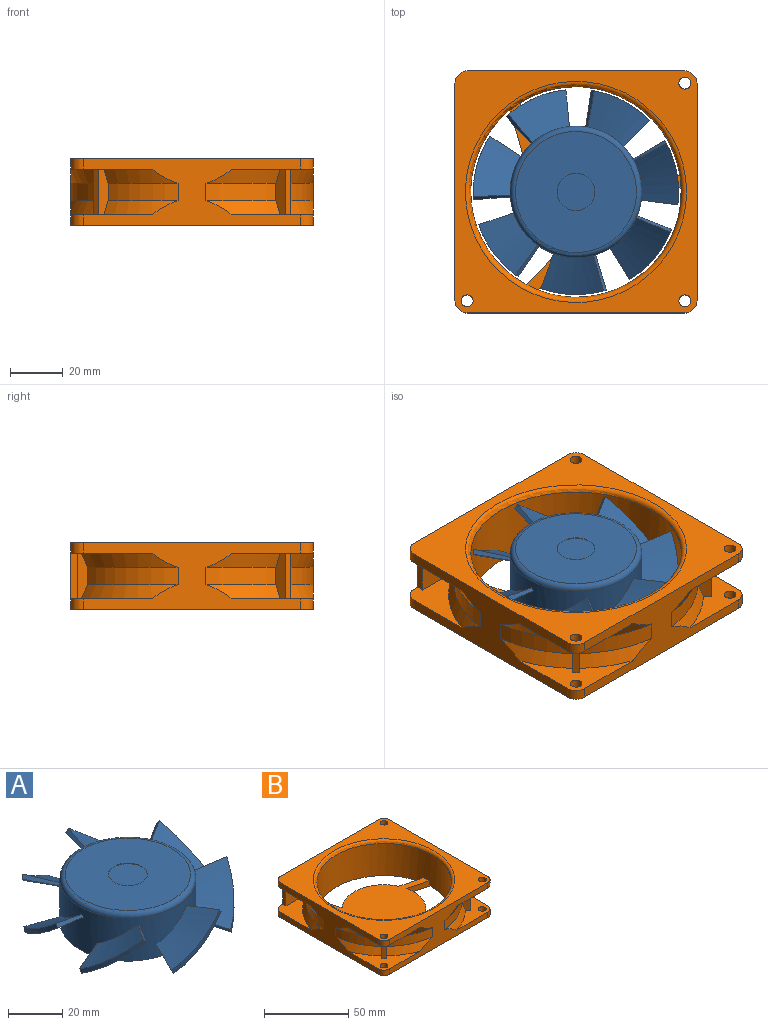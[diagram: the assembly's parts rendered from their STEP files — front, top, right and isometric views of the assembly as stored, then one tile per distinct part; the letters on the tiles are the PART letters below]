
ASSEMBLY  parts=2 mates=1
PART A: 41 faces, bbox 82.4x80.7x21.5 mm
  f0: cylinder r=39mm len=24.46mm, axis (0,0,-1), area 55.4mm2, adj f23,f24,f25,f26
  f1: cylinder r=7.14mm len=14.28mm, axis (0,0,1), area 11.2mm2, adj f32,f33
  f2: torus R=23mm, axis (0,0,-1), area 479.1mm2, adj f3,f33
  f3: cylinder r=25mm len=50mm, axis (0,0,1), area 2885.5mm2, adj f2,f4,f6,f7,f8,f9,f10,f11
  f4: plane 50x50mm, normal (0,0,-1), area 1963.5mm2, adj f3
  f5: cylinder r=39mm len=20.03mm, axis (0,0,-1), area 56.1mm2, adj f6,f7,f8,f9
  f6: bspline ~25.09x24.29mm, area 335.7mm2, adj f3,f5,f7,f9
  f7: plane 11.91x8.96mm, normal (0.71,-0.36,0.6), area 22.3mm2, adj f3,f5,f6,f8
  f8: bspline ~38.56x33.79mm, area 340.4mm2, adj f3,f5,f7,f9
  f9: plane 13.5x5.1mm, normal (-0.2,0.88,-0.44), area 22.3mm2, adj f3,f5,f6,f8
  f10: bspline ~24.11x19.98mm, area 335.6mm2, adj f3,f11,f13,f39
  f11: plane 14.06x4.13mm, normal (0.16,-0.78,0.6), area 22.3mm2, adj f3,f10,f12,f39
  f12: bspline ~41.55x24.68mm, area 340.4mm2, adj f3,f11,f13,f39
  f13: plane 12.23x8.31mm, normal (0.56,0.7,-0.44), area 22.3mm2, adj f3,f10,f12,f39
  f14: cylinder r=39mm len=22.82mm, axis (0,0,-1), area 56.1mm2, adj f15,f16,f17,f18
  f15: bspline ~24.34x22.05mm, area 335.7mm2, adj f3,f14,f16,f18
  f16: plane 11.14x9.97mm, normal (-0.51,-0.61,0.6), area 22.3mm2, adj f3,f14,f15,f17
  f17: bspline ~40.56x27.69mm, area 340.4mm2, adj f3,f14,f16,f18
  f18: plane 14x4.39mm, normal (0.9,0,-0.44), area 22.3mm2, adj f3,f14,f15,f17
  f19: bspline ~40.48x30.08mm, area 335.6mm2, adj f3,f20,f22,f40
  f20: plane 13.98x4.13mm, normal (-0.8,0.02,0.6), area 22.3mm2, adj f3,f19,f21,f40
  f21: bspline ~41.09x29.24mm, area 340.4mm2, adj f3,f20,f22,f40
  f22: plane 10.64x10.36mm, normal (0.56,-0.71,-0.44), area 22.3mm2, adj f3,f19,f21,f40
  f23: bspline ~40.7x24.57mm, area 335.5mm2, adj f0,f3,f24,f26
  f24: plane 12.76x7.52mm, normal (-0.48,0.64,0.6), area 22.3mm2, adj f0,f3,f23,f25
  f25: bspline ~40.53x24.91mm, area 340.3mm2, adj f0,f3,f24,f26
  f26: plane 13.98x4.39mm, normal (-0.2,-0.88,-0.44), area 22.3mm2, adj f0,f3,f23,f25
  f27: cylinder r=39mm len=18.88mm, axis (0,0,-1), area 56.1mm2, adj f28,f29,f30,f31
  f28: bspline ~25.31x24.59mm, area 335.7mm2, adj f3,f27,f29,f31
  f29: plane 13.27x6.34mm, normal (0.2,0.78,0.6), area 22.3mm2, adj f3,f27,f28,f30
  f30: bspline ~38.19x34.62mm, area 340.4mm2, adj f3,f27,f29,f31
  f31: plane 12.32x7.87mm, normal (-0.81,-0.39,-0.44), area 22.3mm2, adj f3,f27,f28,f30
  f32: plane 14.28x14.28mm, normal (0,0,1), area 160.2mm2, adj f1
  f33: plane 46x46mm, normal (0,0,1), area 1501.7mm2, adj f1,f2
  f34: cylinder r=39mm len=24.88mm, axis (0,0,-1), area 56.1mm2, adj f35,f36,f37,f38
  f35: plane 13.39x5.47mm, normal (-0.81,0.39,-0.44), area 22.3mm2, adj f3,f34,f36,f38
  f36: bspline ~24.96x16.85mm, area 339.2mm2, adj f3,f34,f35,f37
  f37: plane 13.74x4.69mm, normal (0.73,0.33,0.6), area 22.3mm2, adj f3,f34,f36,f38
  f38: bspline ~39.52x25.31mm, area 344mm2, adj f3,f34,f35,f37
  f39: bspline ~25.26x18.91mm, area 55.6mm2, adj f10,f11,f12,f13
  f40: bspline ~23.14x18.91mm, area 55.6mm2, adj f19,f20,f21,f22
PART B: 79 faces, bbox 96.3x96.3x25.4 mm
  f0: cylinder r=2.28mm len=4.55mm, axis (0,0,-1), area 57.2mm2, adj f26,f75
  f1: cylinder r=2.28mm len=4.55mm, axis (0,0,-1), area 57.2mm2, adj f28,f72
  f2: cylinder r=2.28mm len=4.55mm, axis (0,0,-1), area 57.2mm2, adj f49,f72
  f3: cylinder r=2.28mm len=4.55mm, axis (0,0,-1), area 57.2mm2, adj f58,f75
  f4: cylinder r=2.28mm len=4.55mm, axis (0,0,-1), area 57.2mm2, adj f64,f72
  f5: cylinder r=25mm len=38.37mm, axis (0,0,-1), area 188.1mm2, adj f70,f71,f72,f74
  f6: cylinder r=40mm len=80mm, axis (0,0,-1), area 5823.8mm2, adj f7,f66,f67,f69,f70,f71,f72,f73
  f7: torus R=42mm, axis (0,0,1), area 803.9mm2, adj f6,f75
  f8: cylinder r=2.28mm len=4.55mm, axis (0,0,-1), area 57.2mm2, adj f75,f76
  f9: cylinder r=4.75mm len=4.75mm, axis (0,0,-1), area 29.8mm2, adj f43,f53,f75,f76
  f10: cylinder r=4.75mm len=4.75mm, axis (0,0,-1), area 29.8mm2, adj f43,f49,f53,f72
  f11: plane 6.18x2.54mm, normal (0,0,-1), area 7.3mm2, adj f12,f16,f35
  f12: cone r=48.47mm half-angle=22deg, axis (0,0,1), area 64.1mm2, adj f11,f13,f16,f35
  f13: cylinder r=46.3mm len=16.15mm, axis (0,0,1), area 113.6mm2, adj f12,f14,f16,f35
  f14: cone r=46.3mm half-angle=22deg, axis (0,0,-1), area 64.1mm2, adj f13,f15,f16,f35
  f15: plane 6.18x2.54mm, normal (0,0,1), area 7.3mm2, adj f14,f16,f35
  f16: plane 17.43x4.99mm, normal (1,0,0), area 73.3mm2, adj f11,f12,f13,f14,f15,f35
  f17: cylinder r=4.75mm len=4.75mm, axis (0,0,-1), area 29.8mm2, adj f31,f53,f58,f75
  f18: cone r=48.47mm half-angle=22deg, axis (0,0,1), area 143.5mm2, adj f19,f21,f26,f35
  f19: cylinder r=46.3mm len=26.58mm, axis (0,0,1), area 199.5mm2, adj f18,f20,f21,f35
  f20: cone r=46.3mm half-angle=22deg, axis (0,0,-1), area 143.5mm2, adj f19,f21,f28,f35
  f21: plane 17.4x3.67mm, normal (-0.71,0.71,0), area 78.7mm2, adj f18,f19,f20,f26,f27,f28
  f22: plane 17.4x3.67mm, normal (0.71,-0.71,0), area 78.7mm2, adj f23,f24,f25,f26,f27,f28
  f23: cone r=46.3mm half-angle=22deg, axis (0,0,-1), area 143.5mm2, adj f22,f24,f28,f31
  f24: cylinder r=46.3mm len=26.58mm, axis (0,0,1), area 199.5mm2, adj f22,f23,f25,f31
  f25: cone r=48.47mm half-angle=22deg, axis (0,0,1), area 143.5mm2, adj f22,f24,f26,f31
  f26: plane 30.73x30.73mm, normal (0,0,-1), area 293.1mm2, adj f0,f18,f21,f22,f25,f27,f31,f32
  f27: plane 17.4x1.71mm, normal (0.71,0.71,0), area 42mm2, adj f21,f22,f26,f28
  f28: plane 30.73x30.73mm, normal (0,0,1), area 293.1mm2, adj f1,f20,f21,f22,f23,f27,f29,f31
  f29: cylinder r=4.75mm len=4.75mm, axis (0,0,-1), area 29.8mm2, adj f28,f31,f35,f72
  f30: cylinder r=4.75mm len=4.75mm, axis (0,0,-1), area 29.8mm2, adj f31,f53,f64,f72
  f31: plane 82.5x25.4mm, normal (1,0,0), area 967.6mm2, adj f17,f23,f24,f25,f26,f28,f29,f30
  f32: cylinder r=4.75mm len=4.75mm, axis (0,0,-1), area 29.8mm2, adj f26,f31,f35,f75
  f33: cylinder r=4.75mm len=4.75mm, axis (0,0,-1), area 29.8mm2, adj f35,f42,f43,f75
  f34: cylinder r=4.75mm len=4.75mm, axis (0,0,-1), area 29.8mm2, adj f35,f40,f43,f72
  f35: plane 82.5x25.4mm, normal (0,1,0), area 1274.8mm2, adj f11,f12,f13,f14,f15,f16,f18,f19
  f36: plane 17.4x2.6mm, normal (-1,0,0), area 45.2mm2, adj f35,f40,f41,f42
  f37: cone r=48.47mm half-angle=22deg, axis (0,0,1), area 219.7mm2, adj f38,f42,f43,f78
  f38: cylinder r=46.3mm len=34.27mm, axis (0,0,1), area 281.6mm2, adj f37,f39,f43,f78
  f39: cone r=46.3mm half-angle=22deg, axis (0,0,-1), area 219.7mm2, adj f38,f40,f43,f78
  f40: plane 30.73x21.95mm, normal (0,0,1), area 261.8mm2, adj f34,f35,f36,f39,f41,f43,f78
  f41: plane 17.4x15.05mm, normal (0,-1,0), area 261.9mm2, adj f36,f40,f42,f78
  f42: plane 30.73x21.95mm, normal (0,0,-1), area 261.8mm2, adj f33,f35,f36,f37,f41,f43,f78
  f43: plane 82.5x25.4mm, normal (-1,0,0), area 967.7mm2, adj f9,f10,f33,f34,f37,f38,f39,f40
  f44: cone r=46.3mm half-angle=22deg, axis (0,0,-1), area 143.5mm2, adj f43,f45,f47,f49
  f45: cylinder r=46.3mm len=26.58mm, axis (0,0,1), area 199.5mm2, adj f43,f44,f46,f47
  f46: cone r=48.47mm half-angle=22deg, axis (0,0,1), area 143.5mm2, adj f43,f45,f47,f76
  f47: plane 17.4x3.67mm, normal (-0.71,0.71,0), area 78.7mm2, adj f44,f45,f46,f48,f49,f76
  f48: plane 17.4x1.71mm, normal (-0.71,-0.71,0), area 42mm2, adj f47,f49,f76,f77
  f49: plane 30.73x30.73mm, normal (0,0,1), area 293.1mm2, adj f2,f10,f43,f44,f47,f48,f50,f53
  f50: cone r=46.3mm half-angle=22deg, axis (0,0,-1), area 143.5mm2, adj f49,f51,f53,f77
  f51: cylinder r=46.3mm len=26.58mm, axis (0,0,1), area 199.5mm2, adj f50,f52,f53,f77
  f52: cone r=48.47mm half-angle=22deg, axis (0,0,1), area 143.5mm2, adj f51,f53,f76,f77
  f53: plane 82.5x25.4mm, normal (0,-1,0), area 967.6mm2, adj f9,f10,f17,f30,f49,f50,f51,f52
  f54: plane 17.4x3.67mm, normal (-0.71,-0.71,0), area 78.7mm2, adj f55,f56,f57,f58,f63,f64
  f55: cone r=46.3mm half-angle=22deg, axis (0,0,-1), area 143.5mm2, adj f53,f54,f56,f64
  f56: cylinder r=46.3mm len=26.58mm, axis (0,0,1), area 199.5mm2, adj f53,f54,f55,f57
  f57: cone r=48.47mm half-angle=22deg, axis (0,0,1), area 143.5mm2, adj f53,f54,f56,f58
  f58: plane 30.73x30.73mm, normal (0,0,-1), area 293.1mm2, adj f3,f17,f31,f53,f54,f57,f59,f62
  f59: cone r=48.47mm half-angle=22deg, axis (0,0,1), area 143.5mm2, adj f31,f58,f60,f62
  f60: cylinder r=46.3mm len=26.58mm, axis (0,0,1), area 199.5mm2, adj f31,f59,f61,f62
  f61: cone r=46.3mm half-angle=22deg, axis (0,0,-1), area 143.5mm2, adj f31,f60,f62,f64
  f62: plane 17.4x3.67mm, normal (0.71,0.71,0), area 78.7mm2, adj f58,f59,f60,f61,f63,f64
  f63: plane 17.4x1.71mm, normal (0.71,-0.71,0), area 42mm2, adj f54,f58,f62,f64
  f64: plane 30.73x30.73mm, normal (0,0,1), area 293.1mm2, adj f4,f30,f31,f53,f54,f55,f61,f62
  f65: cylinder r=25mm len=30.24mm, axis (0,0,-1), area 188.1mm2, adj f66,f72,f73,f74
  f66: plane 15.53x4mm, normal (-0.24,-0.97,0), area 64mm2, adj f6,f65,f72,f74
  f67: plane 16.75x4.18mm, normal (0.24,0.97,0), area 69mm2, adj f6,f68,f72,f74
  f68: cylinder r=25mm len=39.54mm, axis (0,0,-1), area 188.1mm2, adj f67,f69,f72,f74
  f69: plane 15.39x4.41mm, normal (0.96,0.28,0), area 64mm2, adj f6,f68,f72,f74
  f70: plane 16.59x4.76mm, normal (-0.96,-0.28,0), area 69mm2, adj f5,f6,f72,f74
  f71: plane 11.51x11.12mm, normal (-0.72,0.69,0), area 64mm2, adj f5,f6,f72,f74
  f72: plane 92x92mm, normal (0,0,-1), area 5556.4mm2, adj f1,f2,f4,f5,f6,f10,f29,f30
  f73: plane 12.42x11.99mm, normal (0.72,-0.69,0), area 69mm2, adj f6,f65,f72,f74
  f74: plane 71.23x65.04mm, normal (0,0,1), area 2187.2mm2, adj f5,f6,f65,f66,f67,f68,f69,f70
  f75: plane 92x92mm, normal (0,0,1), area 2854mm2, adj f0,f3,f7,f8,f9,f17,f31,f32
  f76: plane 30.73x30.73mm, normal (0,0,-1), area 293.1mm2, adj f8,f9,f43,f46,f47,f48,f52,f53
  f77: plane 17.4x3.67mm, normal (0.71,-0.71,0), area 78.7mm2, adj f48,f49,f50,f51,f52,f76
  f78: plane 17.43x3.87mm, normal (-1,0,0), area 53.2mm2, adj f37,f38,f39,f40,f41,f42
PLACE A rot(axis=(0,0,1),52.1deg) t=(29.23,-10.65,0)mm
PLACE B t=(29.23,-10.65,0)mm fixed
MATE revolute A.f0 <-> B.f5  axis (0,0,1) through (29.23,-10.65,25.4)mm
